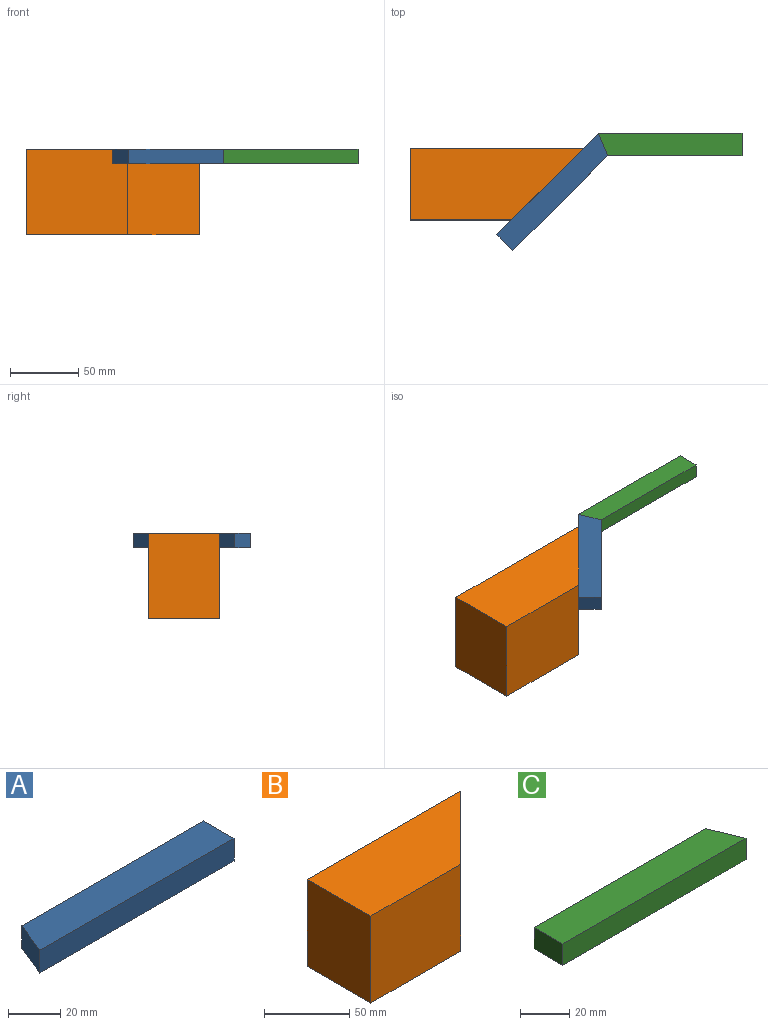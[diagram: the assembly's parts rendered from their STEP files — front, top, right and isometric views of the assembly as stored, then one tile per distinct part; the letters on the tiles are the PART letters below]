
ASSEMBLY  parts=3 mates=2
PART A: 6 faces, bbox 105.3x16.6x10.6 mm
  f0: plane 98.43x10.62mm, normal (0,1,0), area 1045mm2, adj f2,f3,f4,f5
  f1: plane 105.28x10.62mm, normal (0,-1,0), area 1117.8mm2, adj f2,f3,f4,f5
  f2: plane 16.55x10.62mm, normal (1,0,0), area 175.7mm2, adj f0,f1,f3,f4
  f3: plane 105.28x16.55mm, normal (0,0,1), area 1685.8mm2, adj f0,f1,f2,f5
  f4: plane 105.28x16.55mm, normal (0,0,-1), area 1685.8mm2, adj f0,f1,f2,f5
  f5: plane 16.55x10.62mm, normal (-0.92,0.38,0), area 190.2mm2, adj f0,f1,f3,f4
PART B: 6 faces, bbox 127.2x52.7x62.4 mm
  f0: plane 62.43x52.68mm, normal (-1,0,0), area 3288.7mm2, adj f1,f3,f4,f5
  f1: plane 74.53x62.43mm, normal (0,-1,0), area 4652.6mm2, adj f0,f2,f4,f5
  f2: plane 62.43x52.68mm, normal (0.71,-0.71,0), area 4650.9mm2, adj f1,f3,f4,f5
  f3: plane 127.21x62.43mm, normal (0,1,0), area 7941.3mm2, adj f0,f2,f4,f5
  f4: plane 127.21x52.68mm, normal (0,0,1), area 5314mm2, adj f0,f1,f2,f3
  f5: plane 127.21x52.68mm, normal (0,0,-1), area 5314mm2, adj f0,f1,f2,f3
PART C: 6 faces, bbox 105.3x16.6x10.6 mm
  f0: plane 105.28x16.55mm, normal (0,0,1), area 1685.8mm2, adj f2,f3,f4,f5
  f1: plane 105.28x16.55mm, normal (0,0,-1), area 1685.8mm2, adj f2,f3,f4,f5
  f2: plane 98.43x10.62mm, normal (0,1,0), area 1045mm2, adj f0,f1,f3,f5
  f3: plane 16.55x10.62mm, normal (-1,0,0), area 175.7mm2, adj f0,f1,f2,f4
  f4: plane 105.28x10.62mm, normal (0,-1,0), area 1117.8mm2, adj f0,f1,f3,f5
  f5: plane 16.55x10.62mm, normal (0.92,0.38,0), area 190.2mm2, adj f0,f1,f2,f4
PLACE A rot(axis=(0,0,-1),135deg) t=(75.27,51.86,51.81)mm
PLACE B at identity fixed
PLACE C rot(axis=(0,0,1),180deg) t=(168.85,47.01,51.81)mm
MATE fastened A.f5 <-> C.f5  axis (0.92,0.38,0) through (66.99,55.29,57.12)mm
MATE fastened B.f2 <-> A.f1  axis (0.71,-0.71,0) through (26.34,26.34,62.43)mm
